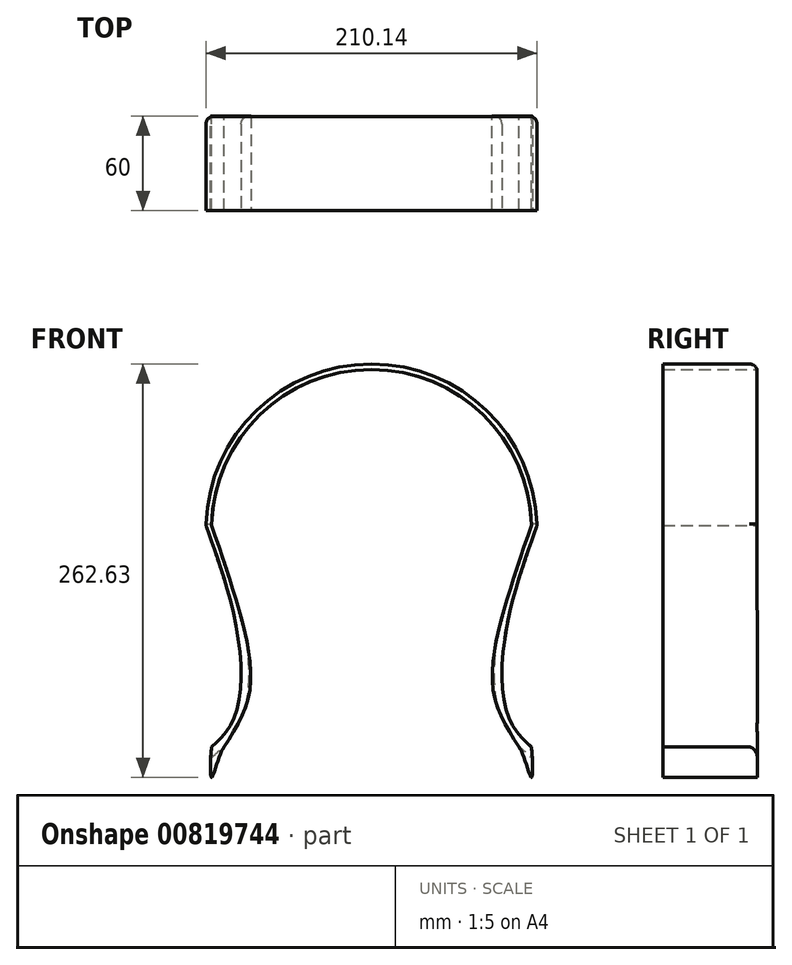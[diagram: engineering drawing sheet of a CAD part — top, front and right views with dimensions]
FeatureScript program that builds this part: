
annotation { "Feature Type Name" : "Feature", "Feature Type Description" : "" }
export const myFeature = defineFeature(function(context is Context, id is Id, definition is map)
    precondition{}
    {
        {
            var Q0;
            Q0=qCreatedBy(makeId("Front.planeOp"),FACE);
            var sketch = newSketch(context, id + "F0", { "sketchPlane" : qUnion([Q0])});
            skArc(sketch, "E0", {"start": v(105.1, 0) * mm, "mid": v(0, 102.63) * mm, "end": v(-105.1, 0) * mm});
            skArc(sketch, "E1", {"start": v(101.6, 0) * mm, "mid": v(0, 99.15) * mm, "end": v(-101.6, 0) * mm});
            skFitSpline(sketch, "E2", {"points": [v(-101.6, 0) * mm, v(-83.3, -56.7) * mm, v(-77.45, -105.3) * mm, v(-93.54, -140.7) * mm], "startDerivative": vector(53.37, -154.3) * mm, "endDerivative": vector(-70.16, -112.8) * mm});
            skFitSpline(sketch, "E3", {"points": [v(-105.1, 0) * mm, v(-98.52, -18.95) * mm, v(-87.4, -56.7) * mm, v(-83.3, -105.3) * mm, v(-91.2, -129.3) * mm, v(-101.6, -140.7) * mm], "startDerivative": vector(36.37, -104.45) * mm, "endDerivative": vector(-74.8, -69.12) * mm});
            skFitSpline(sketch, "E4", {"points": [v(-101.6, -140.7) * mm, v(-101.6, -160) * mm, v(-93.54, -140.7) * mm], "startDerivative": vector(-3.04, -17.82) * mm, "endDerivative": vector(18.16, 16.22) * mm});
            skFitSpline(sketch, "E5.MirrorCS", {"points": [v(101.6, 0) * mm, v(83.3, -56.7) * mm, v(77.45, -105.3) * mm, v(93.54, -140.7) * mm], "startDerivative": vector(-53.37, -154.3) * mm, "endDerivative": vector(70.16, -112.8) * mm});
            skFitSpline(sketch, "E6.MirrorCS", {"points": [v(105.1, 0) * mm, v(98.52, -18.95) * mm, v(87.4, -56.7) * mm, v(83.3, -105.3) * mm, v(91.2, -129.3) * mm, v(101.6, -140.7) * mm], "startDerivative": vector(-36.37, -104.45) * mm, "endDerivative": vector(74.8, -69.12) * mm});
            skFitSpline(sketch, "E7.MirrorCS", {"points": [v(101.6, -140.7) * mm, v(101.6, -160) * mm, v(93.54, -140.7) * mm], "startDerivative": vector(3.04, -17.82) * mm, "endDerivative": vector(-18.16, 16.22) * mm});
            skSolve(sketch);
        }
        {
            var Q0;
            Q0=makeQuery(id+"F0.imprint","IMPRINT",FACE,{"disambiguationData":[TD([[makeQuery(id+"F0.imprint","IMPRINT",EDGE,{"derivedFrom":sQuery(id+"F0.wireOp",EDGE,"E0")}),1.0]])]});
            extrude(context, id + "F1", {"entities" : qUnion([Q0]), "depth" : 60 * mm, "offsetDistance" : 25 * mm});
        }
        {
            var Q0;
            Q0=makeQuery(id+"F1.opExtrude","CAP_EDGE",EDGE,{"disambiguationData":[OSD([sQuery(id+"F0.wireOp",EDGE,"E0")])],"isStart":true});
            fillet(context, id + "F2", {"entities" : qUnion([Q0]), "radius" : 5 * mm, "tangentPropagation" : true, "allowEdgeOverflow" : false});
        }
        {
            var Q0;
            Q0=makeQuery(id+"F1.opExtrude","CAP_EDGE",EDGE,{"disambiguationData":[OSD([sQuery(id+"F0.wireOp",EDGE,"E6.MirrorCS")])],"isStart":true});
            fillet(context, id + "F3", {"entities" : qUnion([Q0]), "radius" : 5 * mm, "tangentPropagation" : true, "allowEdgeOverflow" : false});
        }
        {
            var Q0;
            Q0=makeQuery(id+"F1.opExtrude","CAP_EDGE",EDGE,{"disambiguationData":[OSD([sQuery(id+"F0.wireOp",EDGE,"E3")])],"isStart":true});
            fillet(context, id + "F4", {"entities" : qUnion([Q0]), "radius" : 5 * mm, "tangentPropagation" : true, "allowEdgeOverflow" : false});
        }
    });
